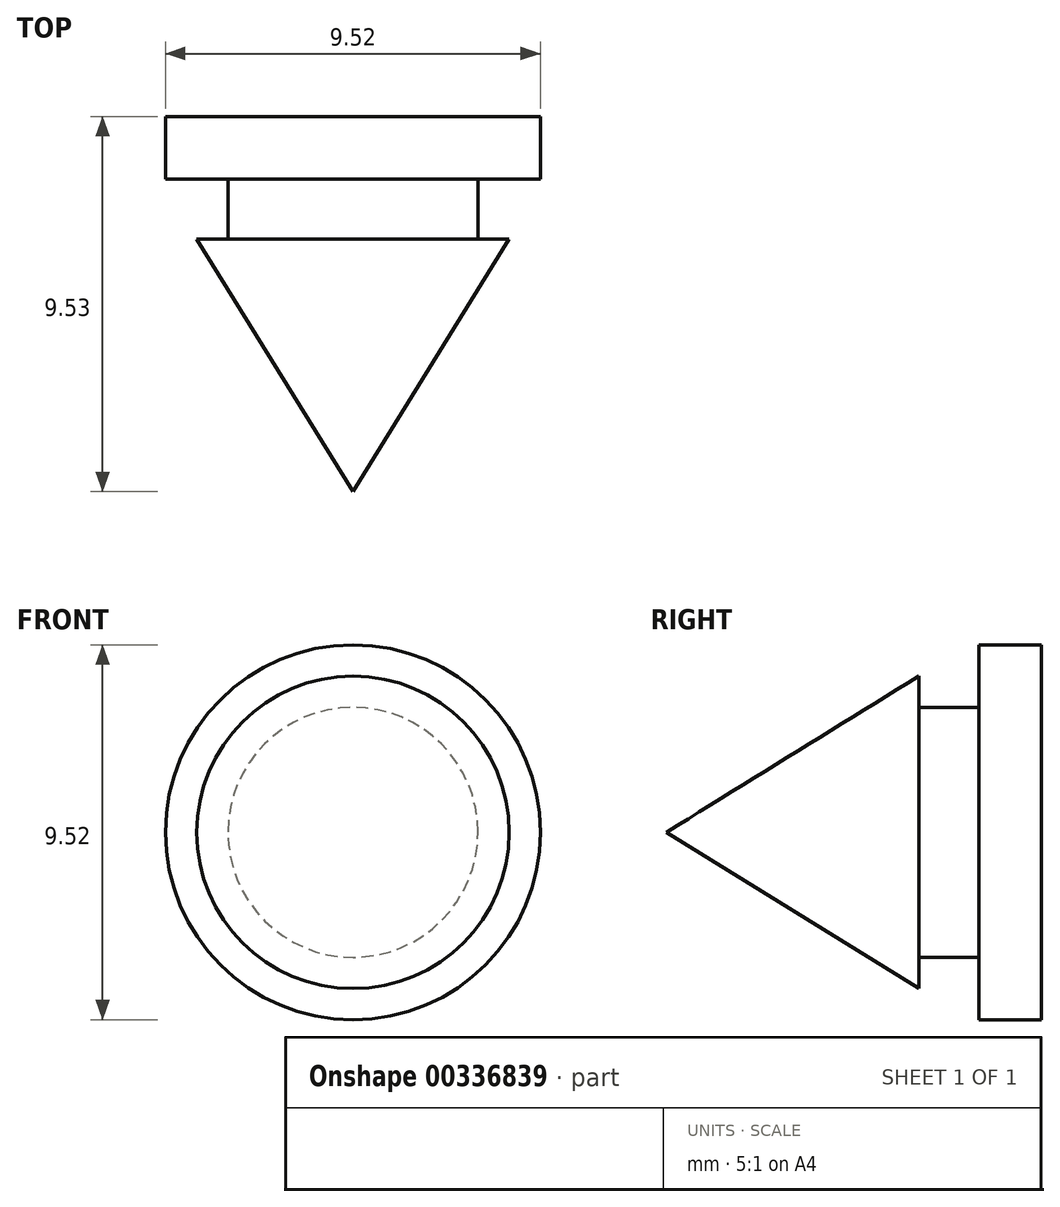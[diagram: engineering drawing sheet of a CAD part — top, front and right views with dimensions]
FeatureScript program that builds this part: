
annotation { "Feature Type Name" : "Feature", "Feature Type Description" : "" }
export const myFeature = defineFeature(function(context is Context, id is Id, definition is map)
    precondition{}
    {
        {
            var Q0;
            Q0=qCreatedBy(makeId("Top.planeOp"),FACE);
            var sketch = newSketch(context, id + "F0", { "sketchPlane" : qUnion([Q0])});
            skLineSegment(sketch, "E0", {"start": v(0, 0) * mm, "end": v(0, 9.53) * mm});
            skLineSegment(sketch, "E1", {"start": v(0, 9.53) * mm, "end": v(-4.76, 9.53) * mm});
            skLineSegment(sketch, "E2", {"start": v(-4.76, 9.53) * mm, "end": v(-4.76, 7.94) * mm});
            skLineSegment(sketch, "E3", {"start": v(-4.76, 7.94) * mm, "end": v(-3.18, 7.94) * mm});
            skLineSegment(sketch, "E4", {"start": v(-3.18, 7.94) * mm, "end": v(-3.17, 6.42) * mm});
            skLineSegment(sketch, "E5", {"start": v(-3.18, 6.42) * mm, "end": v(-3.97, 6.42) * mm});
            skLineSegment(sketch, "E6", {"start": v(-3.97, 6.42) * mm, "end": v(0, 0) * mm});
            skSolve(sketch);
        }
        {
            var Q0;
            Q0=makeQuery(id+"F0.imprint","IMPRINT",FACE,{"disambiguationData":[TD([[makeQuery(id+"F0.imprint","IMPRINT",EDGE,{"derivedFrom":sQuery(id+"F0.wireOp",EDGE,"E0")}),1.0]])]});
            var Q1;
            Q1=sQuery(id+"F0.wireOp",EDGE,"E0");
            revolve(context, id + "F1", {"entities" : qUnion([Q0]), "axis" : qUnion([Q1]), "revolveType" : RevolveType.FULL});
        }
    });
